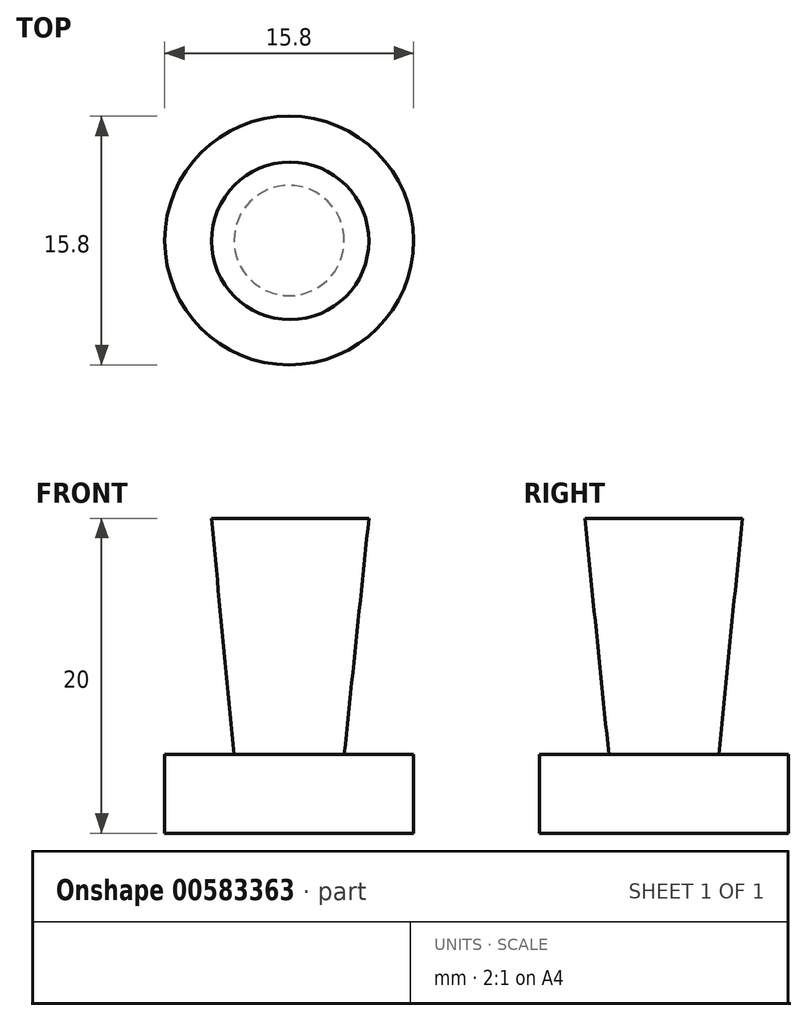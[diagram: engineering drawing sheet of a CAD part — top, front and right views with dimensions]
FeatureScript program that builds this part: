
annotation { "Feature Type Name" : "Feature", "Feature Type Description" : "" }
export const myFeature = defineFeature(function(context is Context, id is Id, definition is map)
    precondition{}
    {
        {
            var Q0;
            Q0=qCreatedBy(makeId("Top.planeOp"),FACE);
            var sketch = newSketch(context, id + "F0", { "sketchPlane" : qUnion([Q0])});
            skCircle(sketch, "E0", {"center": v(-18.68, 1.8) * mm, "radius": 7.9 * mm});
            skSolve(sketch);
        }
        {
            var Q0;
            Q0 = qSketchRegion(id + "F0", true);
            extrude(context, id + "F1", {"entities" : qUnion([Q0]), "depth" : 5 * mm, "offsetDistance" : 25 * mm});
        }
        {
            var Q0;
            Q0=makeQuery(id+"F1.opExtrude","CAP_FACE",FACE,{"disambiguationData":[OSD([sQuery(id+"F0.wireOp",EDGE,"E0")])],"isStart":false});
            var sketch = newSketch(context, id + "F2", { "sketchPlane" : qUnion([Q0])});
            skCircle(sketch, "E1", {"center": v(-18.68, 1.8) * mm, "radius": 3.5 * mm});
            skSolve(sketch);
        }
        {
            var Q0;
            Q0=qCreatedBy(makeId("Top.planeOp"),FACE);
            cPlane(context, id + "F3", {"entities" : qUnion([Q0]), "cplaneType" : CPlaneType.OFFSET, "offset" : 20 * mm, "width" : 150 * mm, "height" : 150 * mm});
        }
        {
            var Q0;
            Q0=qCreatedBy(id+"F3.planeOp",FACE);
            var sketch = newSketch(context, id + "F4", { "sketchPlane" : qUnion([Q0])});
            skCircle(sketch, "E2", {"center": v(-18.62, 1.77) * mm, "radius": 5 * mm});
            skSolve(sketch);
        }
        {
            var Q1;
            Q1=makeQuery(id+"F4.imprint","IMPRINT",FACE,{"disambiguationData":[TD([[makeQuery(id+"F4.imprint","IMPRINT",EDGE,{"derivedFrom":sQuery(id+"F4.wireOp",EDGE,"E2")}),1.0]])]});
            var Q2;
            Q2=makeQuery(id+"F2.imprint","IMPRINT",FACE,{"disambiguationData":[TD([[makeQuery(id+"F2.imprint","IMPRINT",EDGE,{"derivedFrom":sQuery(id+"F2.wireOp",EDGE,"E1")}),1.0]])]});
            loft(context, id + "F5", {"operationType" : NewBodyOperationType.ADD, "sheetProfilesArray" : [{ "sheetProfileEntities" : qUnion([Q1]) }, { "sheetProfileEntities" : qUnion([Q2]) }]});
        }
    });
